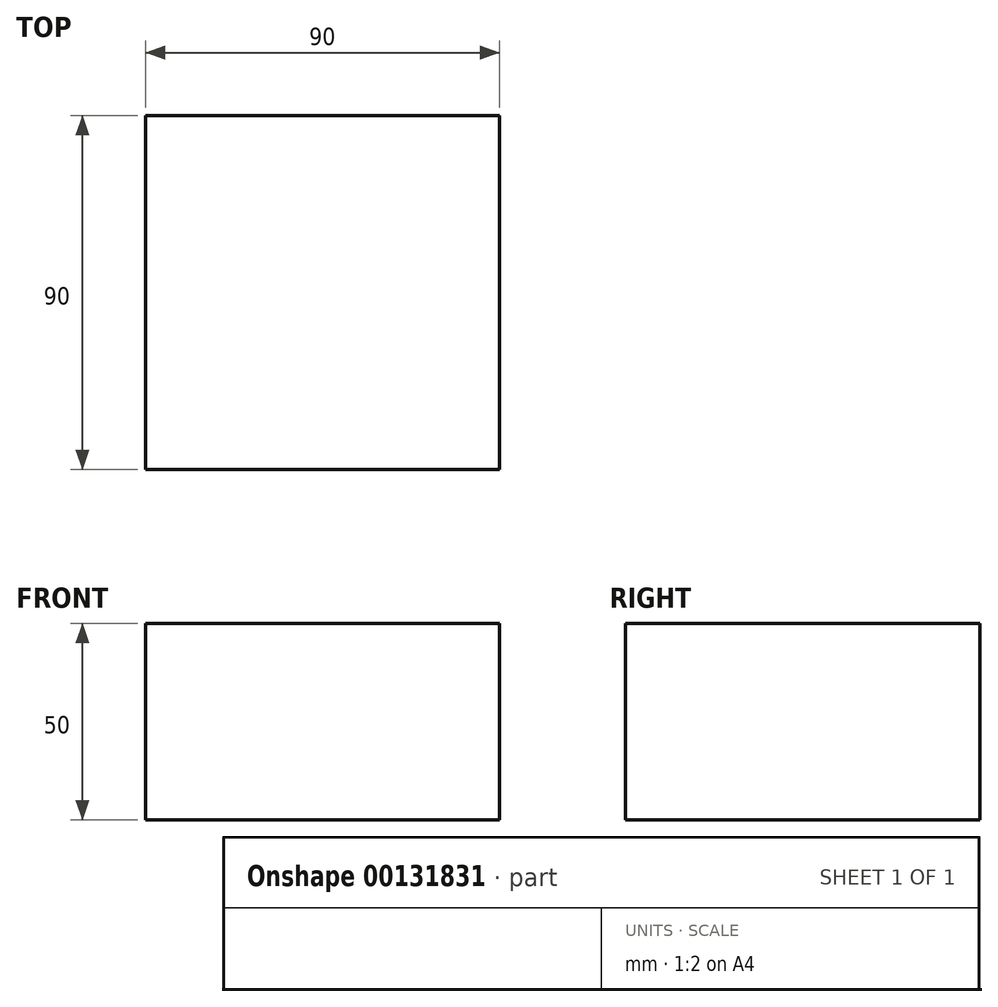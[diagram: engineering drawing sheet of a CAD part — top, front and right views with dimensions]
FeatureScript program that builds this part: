
annotation { "Feature Type Name" : "Feature", "Feature Type Description" : "" }
export const myFeature = defineFeature(function(context is Context, id is Id, definition is map)
    precondition{}
    {
        {
            var Q0;
            Q0=qCreatedBy(makeId("Top.planeOp"),FACE);
            var sketch = newSketch(context, id + "F0", { "sketchPlane" : qUnion([Q0])});
            skLineSegment(sketch, "E0.bottom", {"start": v(48.1, -11.94) * mm, "end": v(-41.9, -11.94) * mm});
            skLineSegment(sketch, "E0.top", {"start": v(48.1, 78.06) * mm, "end": v(-41.9, 78.06) * mm});
            skLineSegment(sketch, "E0.left", {"start": v(48.1, -11.94) * mm, "end": v(48.1, 78.06) * mm});
            skLineSegment(sketch, "E0.right", {"start": v(-41.9, -11.94) * mm, "end": v(-41.9, 78.06) * mm});
            skSolve(sketch);
        }
        {
            var Q0;
            Q0 = qSketchRegion(id + "F0", true);
            extrude(context, id + "F1", {"entities" : qUnion([Q0]), "depth" : 50 * mm});
        }
    });
